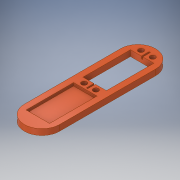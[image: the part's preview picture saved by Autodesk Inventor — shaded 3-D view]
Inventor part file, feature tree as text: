
AUTODESK INVENTOR PART (.ipt)
format: ipt  version: 2017 (Build 210142000, 142)  size: 168,448 bytes
history: native  units: mm
features: extrude x5, sketch x4, fillet x2
ambient origin geometry x8: Origin, YZ Plane, XZ Plane, XY Plane, X Axis, Y Axis, Z Axis, Center Point
bodies: Solid1 (feature_tree)
feature tree (11):
  extrude  "Extrusion1"  Depth=30.0mm
  sketch  "Sketch2"  dims[d2=5.0mm d3=0.0mm]
  extrude  "Extrusion2"  TaperAngle=0.0deg  [1 undecoded]
  extrude  "Extrusion3"  Depth=20.0mm
  extrude  "Extrusion4"  Depth=2.0mm
  extrude  "Extrusion5"  Depth=5.0mm
  fillet  "Fillet1"  [1 undecoded]
  fillet  "Fillet2"  Radius=2.5mm
  sketch  "Sketch1"  dims[d0=30.0mm d1=112.0mm]
  sketch  "Sketch3"  dims[d4=5.0mm d5=20.0mm]
  sketch  "Sketch4"  dims[d6=40.5mm d7=11.5mm d8=5.0mm d9=0.0mm d10=2.5mm d11=0.0mm d13=4.0mm d14=4.0mm d15=2.75mm d16=2.75mm d17=4.5mm d18=2.5mm d19=0.0mm d20=6.5mm d21=1.2mm d22=2.0mm d23=0.0mm]
note: 2 required parameter values undecoded (feature->parameter linkage not recoverable at this tier; creation-order binding heuristic only, values carry confidence <= 0.55)
